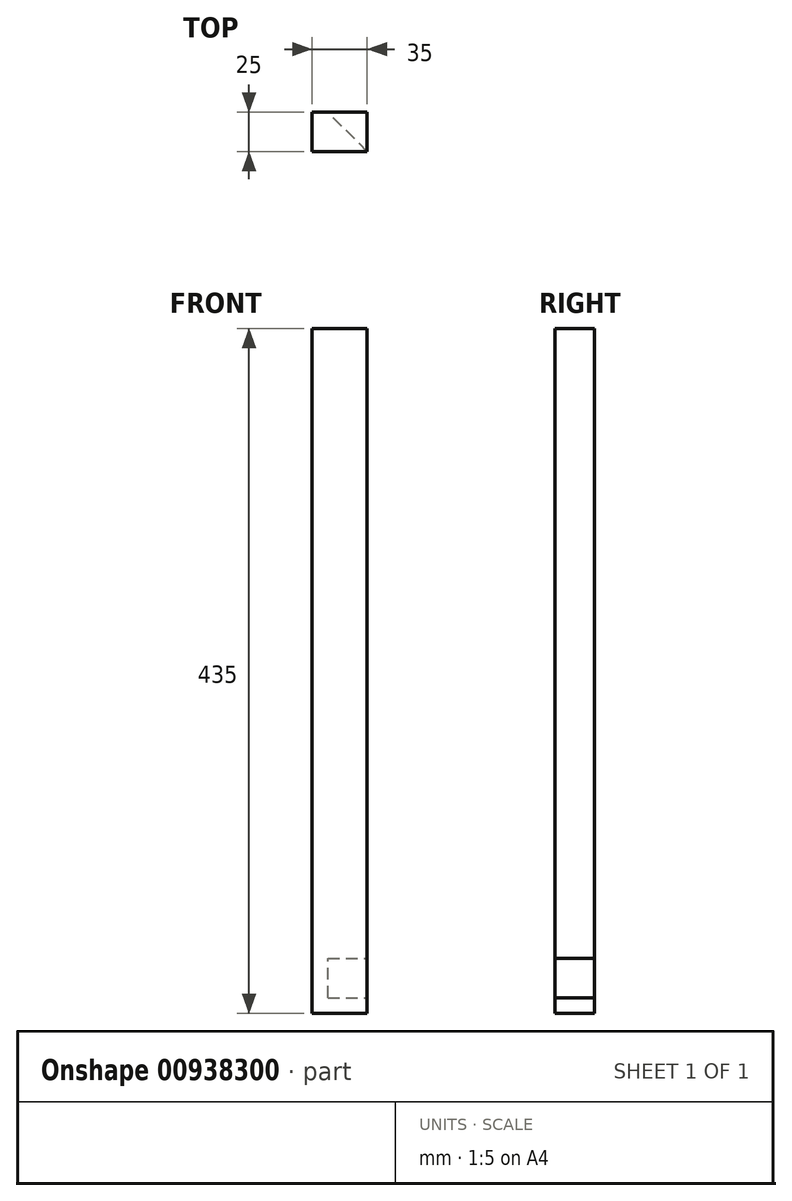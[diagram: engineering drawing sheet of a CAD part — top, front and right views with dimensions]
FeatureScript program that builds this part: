
annotation { "Feature Type Name" : "Feature", "Feature Type Description" : "" }
export const myFeature = defineFeature(function(context is Context, id is Id, definition is map)
    precondition{}
    {
        {
            var Q0;
            Q0=qCreatedBy(makeId("Top.planeOp"),FACE);
            var sketch = newSketch(context, id + "F0", { "sketchPlane" : qUnion([Q0])});
            skLineSegment(sketch, "E0.bottom", {"start": v(-59.86, -35.75) * mm, "end": v(-24.86, -35.75) * mm});
            skLineSegment(sketch, "E0.top", {"start": v(-59.86, -60.75) * mm, "end": v(-24.86, -60.75) * mm});
            skLineSegment(sketch, "E0.left", {"start": v(-59.86, -35.75) * mm, "end": v(-59.86, -60.75) * mm});
            skLineSegment(sketch, "E0.right", {"start": v(-24.86, -35.75) * mm, "end": v(-24.86, -60.75) * mm});
            skSolve(sketch);
        }
        {
            var Q0;
            Q0=makeQuery(id+"F0.imprint","IMPRINT",FACE,{"disambiguationData":[TD([[makeQuery(id+"F0.imprint","IMPRINT",EDGE,{"derivedFrom":sQuery(id+"F0.wireOp",EDGE,"E0.bottom")}),-1.0]])]});
            extrude(context, id + "F1", {"entities" : qUnion([Q0]), "depth" : 400 * mm, "offsetDistance" : 25 * mm});
        }
        {
            var Q0;
            Q0=makeQuery(id+"F1.opExtrude","CAP_FACE",FACE,{"disambiguationData":[OSD([sQuery(id+"F0.wireOp",EDGE,"E0.bottom"),sQuery(id+"F0.wireOp",EDGE,"E0.top"),sQuery(id+"F0.wireOp",EDGE,"E0.left"),sQuery(id+"F0.wireOp",EDGE,"E0.right")])],"isStart":true});
            var sketch = newSketch(context, id + "F2", { "sketchPlane" : qUnion([Q0])});
            skLineSegment(sketch, "E1", {"start": v(-24.86, 60.75) * mm, "end": v(-49.86, 35.75) * mm});
            skLineSegment(sketch, "E2", {"start": v(-49.86, 35.75) * mm, "end": v(-59.86, 35.75) * mm});
            skLineSegment(sketch, "E3", {"start": v(-59.86, 35.75) * mm, "end": v(-59.86, 60.75) * mm});
            skLineSegment(sketch, "E4", {"start": v(-59.86, 60.75) * mm, "end": v(-24.86, 60.75) * mm});
            skSolve(sketch);
        }
        {
            var Q0;
            Q0=makeQuery(id+"F2.imprint","IMPRINT",FACE,{"disambiguationData":[TD([[makeQuery(id+"F2.imprint","IMPRINT",EDGE,{"derivedFrom":sQuery(id+"F2.wireOp",EDGE,"E1")}),-1.0]])]});
            extrude(context, id + "F3", {"entities" : qUnion([Q0]), "operationType" : NewBodyOperationType.ADD, "depth" : 25 * mm, "offsetDistance" : 25 * mm});
        }
        {
            var Q0;
            Q0=makeQuery(id+"F3.opExtrude","CAP_FACE",FACE,{"disambiguationData":[OSD([sQuery(id+"F2.wireOp",EDGE,"E1"),sQuery(id+"F2.wireOp",EDGE,"E2"),sQuery(id+"F2.wireOp",EDGE,"E3"),sQuery(id+"F2.wireOp",EDGE,"E4")])],"isStart":false});
            var sketch = newSketch(context, id + "F4", { "sketchPlane" : qUnion([Q0])});
            skLineSegment(sketch, "E5.bottom", {"start": v(-59.86, 60.75) * mm, "end": v(-24.86, 60.75) * mm});
            skLineSegment(sketch, "E5.top", {"start": v(-59.86, 35.75) * mm, "end": v(-24.86, 35.75) * mm});
            skLineSegment(sketch, "E5.left", {"start": v(-59.86, 60.75) * mm, "end": v(-59.86, 35.75) * mm});
            skLineSegment(sketch, "E5.right", {"start": v(-24.86, 60.75) * mm, "end": v(-24.86, 35.75) * mm});
            skSolve(sketch);
        }
        {
            var Q0;
            Q0=makeQuery(id+"F4.imprint","IMPRINT",FACE,{"disambiguationData":[TD([[makeQuery(id+"F4.imprint","IMPRINT",EDGE,{"derivedFrom":sQuery(id+"F4.wireOp",EDGE,"E5.bottom")}),-1.0]])]});
            var Q1;
            {var subQ2=sQuery(id+"F4.wireOp",EDGE,"E5.right");Q1=makeQuery(id+"F4.imprint","IMPRINT",FACE,{"disambiguationData":[TD([[makeQuery(id+"F4.imprint","IMPRINT",EDGE,{"derivedFrom":subQ2}),-1.0]])]});}
            extrude(context, id + "F5", {"entities" : qUnion([Q0, Q1]), "operationType" : NewBodyOperationType.ADD, "depth" : 10 * mm, "offsetDistance" : 25 * mm});
        }
    });
